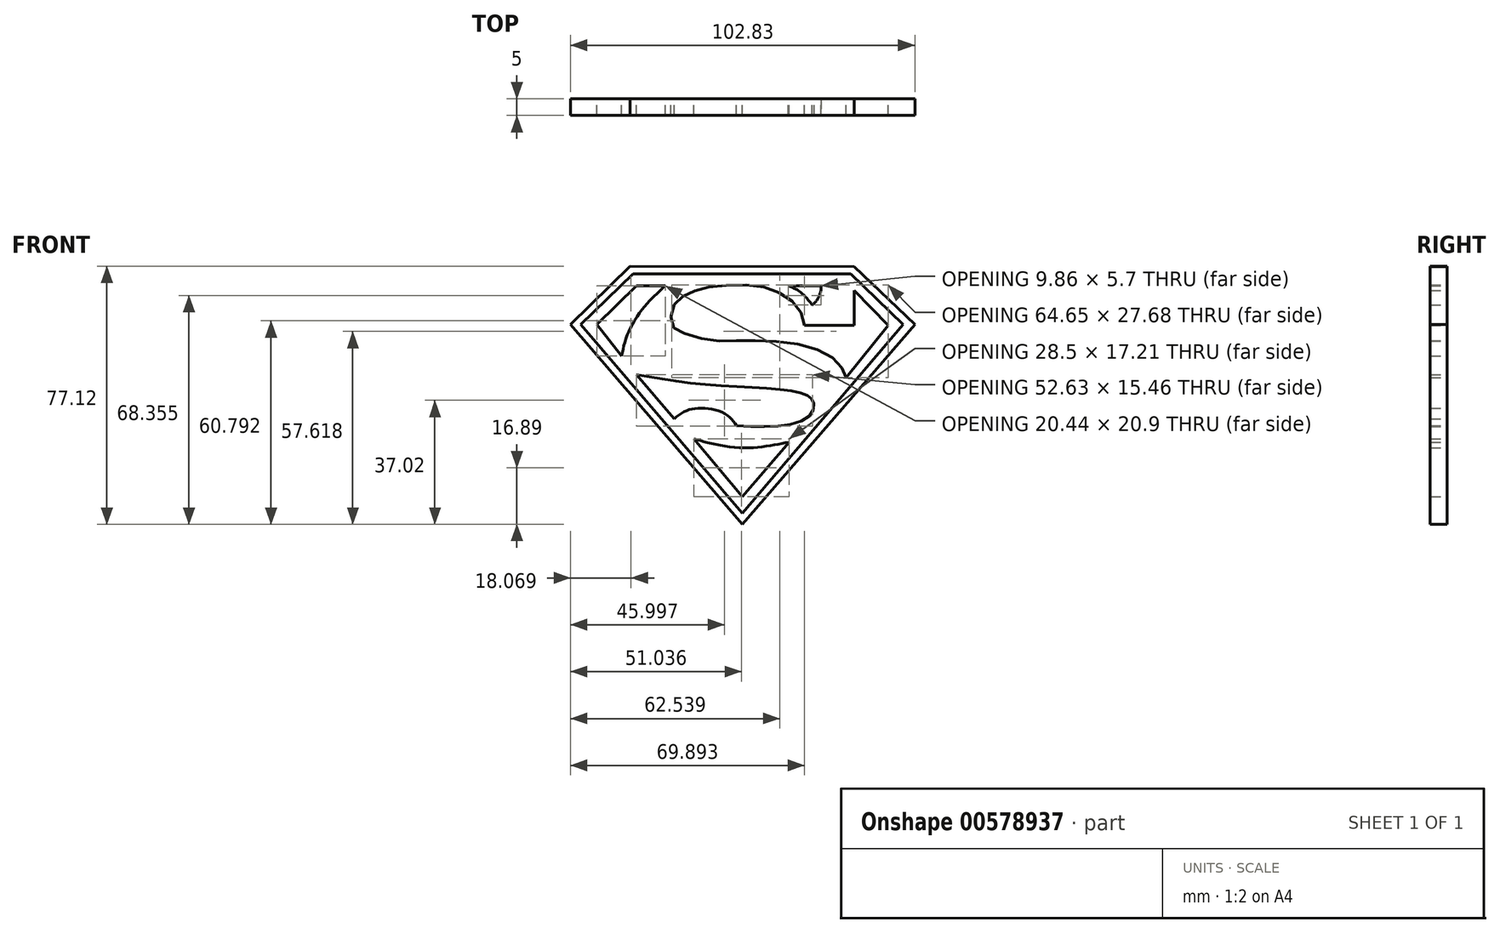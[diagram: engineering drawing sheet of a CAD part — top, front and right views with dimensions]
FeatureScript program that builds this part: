
annotation { "Feature Type Name" : "Feature", "Feature Type Description" : "" }
export const myFeature = defineFeature(function(context is Context, id is Id, definition is map)
    precondition{}
    {
        {
            var Q0;
            Q0=qCreatedBy(makeId("Front.planeOp"),FACE);
            var sketch = newSketch(context, id + "F0", { "sketchPlane" : qUnion([Q0])});
            skFitSpline(sketch, "E0", {"points": [v(-87.65, 79.13) * mm, v(-20.75, 79.03) * mm], "startDerivative": vector(66.9, -0.1) * mm, "endDerivative": vector(66.9, -0.1) * mm});
            skFitSpline(sketch, "E1", {"points": [v(-20.75, 79.03) * mm, v(-2.57, 61.7) * mm], "startDerivative": vector(18.18, -17.32) * mm, "endDerivative": vector(18.18, -17.32) * mm});
            skFitSpline(sketch, "E2", {"points": [v(-87.65, 79.13) * mm, v(-105.4, 61.7) * mm], "startDerivative": vector(-17.75, -17.42) * mm, "endDerivative": vector(-17.75, -17.42) * mm});
            skFitSpline(sketch, "E3", {"points": [v(-105.4, 61.7) * mm, v(-54.1, 2.01) * mm], "startDerivative": vector(51.3, -59.7) * mm, "endDerivative": vector(51.3, -59.7) * mm});
            skFitSpline(sketch, "E4", {"points": [v(-54.1, 2.01) * mm, v(-2.57, 61.7) * mm], "startDerivative": vector(51.52, 59.7) * mm, "endDerivative": vector(51.52, 59.7) * mm});
            skFitSpline(sketch, "E5", {"points": [v(-102.39, 61.7) * mm, v(-86.69, 76.77) * mm], "startDerivative": vector(15.7, 15.06) * mm, "endDerivative": vector(15.7, 15.06) * mm});
            skFitSpline(sketch, "E6", {"points": [v(-86.69, 76.77) * mm, v(-21.72, 76.77) * mm], "startDerivative": vector(64.97, 0) * mm, "endDerivative": vector(64.97, 0) * mm});
            skFitSpline(sketch, "E7", {"points": [v(-21.72, 76.77) * mm, v(-6.12, 61.7) * mm], "startDerivative": vector(15.6, -15.06) * mm, "endDerivative": vector(15.6, -15.06) * mm});
            skFitSpline(sketch, "E8", {"points": [v(-6.12, 61.7) * mm, v(-54.1, 5.35) * mm], "startDerivative": vector(-47.97, -56.36) * mm, "endDerivative": vector(-47.97, -56.36) * mm});
            skFitSpline(sketch, "E9", {"points": [v(-54.1, 5.35) * mm, v(-102.39, 61.7) * mm], "startDerivative": vector(-48.3, 56.36) * mm, "endDerivative": vector(-48.3, 56.36) * mm});
            skFitSpline(sketch, "E10", {"points": [v(-97.55, 61.7) * mm, v(-85.72, 73.25) * mm], "startDerivative": vector(11.83, 11.54) * mm, "endDerivative": vector(11.83, 11.54) * mm});
            skFitSpline(sketch, "E11", {"points": [v(-85.72, 73.25) * mm, v(-77.11, 73.25) * mm], "startDerivative": vector(8.6, 0) * mm, "endDerivative": vector(8.6, 0) * mm});
            skFitSpline(sketch, "E12", {"points": [v(-77.11, 73.25) * mm, v(-80.12, 70.42) * mm, v(-84.53, 65.47) * mm, v(-88.62, 58.05) * mm, v(-90.13, 52.35) * mm], "startDerivative": vector(-14.13, -13.01) * mm, "endDerivative": vector(-4.5, -22.52) * mm});
            skFitSpline(sketch, "E13", {"points": [v(-97.55, 61.7) * mm, v(-90.13, 52.35) * mm], "startDerivative": vector(7.42, -9.36) * mm, "endDerivative": vector(7.42, -9.36) * mm});
            skFitSpline(sketch, "E14", {"points": [v(-85.72, 46.76) * mm, v(-74.42, 33.53) * mm], "startDerivative": vector(11.3, -13.23) * mm, "endDerivative": vector(11.3, -13.23) * mm});
            skFitSpline(sketch, "E15", {"points": [v(-85.72, 46.76) * mm, v(-72.81, 44.6) * mm, v(-55.7, 43.1) * mm, v(-41.19, 42.13) * mm, v(-35.27, 40.73) * mm, v(-33.34, 39.34) * mm, v(-32.7, 37.5) * mm, v(-34.09, 34.39) * mm, v(-42.16, 31.48) * mm, v(-55.82, 31.48) * mm], "startDerivative": vector(87.29, -16.29) * mm, "endDerivative": vector(-97.1, 5.64) * mm});
            skFitSpline(sketch, "E16", {"points": [v(-55.82, 31.48) * mm, v(-57.86, 33.96) * mm, v(-62.16, 36.22) * mm, v(-67.43, 36.65) * mm, v(-71.2, 35.79) * mm, v(-74.42, 33.53) * mm], "startDerivative": vector(-9.96, 14.57) * mm, "endDerivative": vector(-16.14, -13.3) * mm});
            skFitSpline(sketch, "E17", {"points": [v(-68.62, 27.5) * mm, v(-54.1, 10.3) * mm], "startDerivative": vector(14.52, -17.2) * mm, "endDerivative": vector(14.52, -17.2) * mm});
            skFitSpline(sketch, "E18", {"points": [v(-54.1, 10.3) * mm, v(-40.11, 26.54) * mm], "startDerivative": vector(13.98, 16.24) * mm, "endDerivative": vector(13.98, 16.24) * mm});
            skFitSpline(sketch, "E19", {"points": [v(-68.62, 27.5) * mm, v(-63.13, 26.1) * mm, v(-54.1, 24.82) * mm, v(-46.14, 25.46) * mm, v(-40.11, 26.54) * mm], "startDerivative": vector(22.87, -6.27) * mm, "endDerivative": vector(25.29, 4.78) * mm});
            skFitSpline(sketch, "E20", {"points": [v(-33.23, 67.52) * mm, v(-31.72, 69.13) * mm, v(-30.65, 71.82) * mm, v(-30.65, 73.86) * mm], "startDerivative": vector(4.92, 4.4) * mm, "endDerivative": vector(-0.6, 6.28) * mm});
            skFitSpline(sketch, "E21", {"points": [v(-30.58, 73.21) * mm, v(-40.43, 73.21) * mm], "startDerivative": vector(-9.85, 0) * mm, "endDerivative": vector(-9.85, 0) * mm});
            skFitSpline(sketch, "E22", {"points": [v(-40.43, 73.21) * mm, v(-36.89, 71.5) * mm, v(-33.23, 67.52) * mm], "startDerivative": vector(7.92, -2.89) * mm, "endDerivative": vector(6.53, -8.36) * mm});
            skFitSpline(sketch, "E23", {"points": [v(-20.75, 71.82) * mm, v(-20.64, 61.5) * mm], "startDerivative": vector(0.1, -10.33) * mm, "endDerivative": vector(0.1, -10.33) * mm});
            skFitSpline(sketch, "E24", {"points": [v(-20.64, 61.5) * mm, v(-35.6, 61.5) * mm], "startDerivative": vector(-14.95, 0) * mm, "endDerivative": vector(-14.95, 0) * mm});
            skFitSpline(sketch, "E25", {"points": [v(-20.75, 71.82) * mm, v(-10.53, 61.5) * mm], "startDerivative": vector(10.22, -10.33) * mm, "endDerivative": vector(10.22, -10.33) * mm});
            skFitSpline(sketch, "E26", {"points": [v(-10.53, 61.5) * mm, v(-23.12, 45.79) * mm], "startDerivative": vector(-12.58, -15.7) * mm, "endDerivative": vector(-12.58, -15.7) * mm});
            skFitSpline(sketch, "E27", {"points": [v(-23.12, 45.79) * mm, v(-24.62, 49.12) * mm, v(-29.68, 53.32) * mm, v(-41.62, 56.44) * mm, v(-54.42, 56.87) * mm, v(-63.35, 56.98) * mm, v(-72.27, 59.34) * mm, v(-74.96, 61.5) * mm, v(-75.07, 66.12) * mm, v(-72.6, 69.56) * mm, v(-68.19, 71.82) * mm, v(-61.2, 73.21) * mm, v(-49.9, 73.21) * mm, v(-42.59, 70.96) * mm, v(-37.2, 66.33) * mm, v(-35.6, 61.5) * mm], "startDerivative": vector(-23.2, 68.84) * mm, "endDerivative": vector(16.56, -86.92) * mm});
            skFitSpline(sketch, "E28", {"points": [v(-95, 61.42) * mm, v(-84.73, 71.55) * mm], "startDerivative": vector(10.28, 10.13) * mm, "endDerivative": vector(10.28, 10.13) * mm});
            skFitSpline(sketch, "E29", {"points": [v(-84.73, 71.55) * mm, v(-81.6, 71.55) * mm], "startDerivative": vector(3.13, 0) * mm, "endDerivative": vector(3.13, 0) * mm});
            skFitSpline(sketch, "E30", {"points": [v(-81.6, 71.55) * mm, v(-84.73, 67.83) * mm, v(-88.75, 62.02) * mm, v(-90.99, 55.47) * mm], "startDerivative": vector(-10.15, -11.89) * mm, "endDerivative": vector(-4.98, -19) * mm});
            skFitSpline(sketch, "E31", {"points": [v(-95, 61.42) * mm, v(-90.99, 55.47) * mm], "startDerivative": vector(4.02, -5.95) * mm, "endDerivative": vector(4.02, -5.95) * mm});
            skFitSpline(sketch, "E32", {"points": [v(-80.26, 43.85) * mm, v(-74.46, 36.7) * mm], "startDerivative": vector(5.8, -7.15) * mm, "endDerivative": vector(5.8, -7.15) * mm});
            skFitSpline(sketch, "E33", {"points": [v(-74.46, 36.7) * mm, v(-71.2, 37.94) * mm, v(-64.63, 39.23) * mm, v(-56.73, 35.79) * mm, v(-54.35, 33.42) * mm], "startDerivative": vector(14.75, 5.57) * mm, "endDerivative": vector(9.34, -11.21) * mm});
            skFitSpline(sketch, "E34", {"points": [v(-54.35, 33.42) * mm, v(-43.18, 33.42) * mm, v(-36.78, 34.62) * mm, v(-34.24, 37.94) * mm, v(-41.1, 40.13) * mm, v(-55.82, 40.87) * mm, v(-74.46, 42.8) * mm, v(-80.26, 43.85) * mm], "startDerivative": vector(75.42, -0.54) * mm, "endDerivative": vector(-42.21, 8.61) * mm});
            skFitSpline(sketch, "E35", {"points": [v(-63.29, 24.04) * mm, v(-54.35, 13.47) * mm], "startDerivative": vector(8.94, -10.57) * mm, "endDerivative": vector(8.94, -10.57) * mm});
            skFitSpline(sketch, "E36", {"points": [v(-54.35, 13.47) * mm, v(-45.56, 23.45) * mm], "startDerivative": vector(8.79, 9.98) * mm, "endDerivative": vector(8.79, 9.98) * mm});
            skFitSpline(sketch, "E37", {"points": [v(-63.29, 24.04) * mm, v(-54.35, 21.77) * mm, v(-45.56, 23.45) * mm], "startDerivative": vector(17.74, -6.5) * mm, "endDerivative": vector(17.7, 5.34) * mm});
            skFitSpline(sketch, "E38", {"points": [v(-18.9, 67.48) * mm, v(-18.75, 59.49) * mm], "startDerivative": vector(0.15, -8) * mm, "endDerivative": vector(0.15, -8) * mm});
            skFitSpline(sketch, "E39", {"points": [v(-18.75, 59.49) * mm, v(-37.52, 59.49) * mm], "startDerivative": vector(-18.77, 0) * mm, "endDerivative": vector(-18.77, 0) * mm});
            skFitSpline(sketch, "E40", {"points": [v(-18.9, 67.48) * mm, v(-13.1, 61.7) * mm], "startDerivative": vector(5.8, -5.77) * mm, "endDerivative": vector(5.8, -5.77) * mm});
            skFitSpline(sketch, "E41", {"points": [v(-13.1, 61.7) * mm, v(-22.63, 49.66) * mm], "startDerivative": vector(-9.53, -12.05) * mm, "endDerivative": vector(-9.53, -12.05) * mm});
            skFitSpline(sketch, "E42", {"points": [v(-22.63, 49.66) * mm, v(-26.2, 53.68) * mm, v(-34.24, 57.4) * mm, v(-49.43, 59.49) * mm, v(-58.94, 59.49) * mm], "startDerivative": vector(-16.55, 22.32) * mm, "endDerivative": vector(-34.78, -1.05) * mm});
            skFitSpline(sketch, "E43", {"points": [v(-37.52, 59.49) * mm, v(-37.52, 61.7) * mm, v(-39.9, 66.73) * mm, v(-49.43, 71.25) * mm, v(-65.82, 70.66) * mm, v(-72.52, 66.73) * mm, v(-73.11, 62.91) * mm, v(-67, 59.49) * mm, v(-49.43, 59.49) * mm], "startDerivative": vector(3.1, 30.38) * mm, "endDerivative": vector(104.27, 7.97) * mm});
            skSolve(sketch);
        }
        {
            var Q0;
            Q0=makeQuery(id+"F0.imprint","IMPRINT",FACE,{"disambiguationData":[TD([[makeQuery(id+"F0.imprint","IMPRINT",EDGE,{"derivedFrom":sQuery(id+"F0.wireOp",EDGE,"E0")}),-1.0]])]});
            extrude(context, id + "F1", {"entities" : qUnion([Q0]), "depth" : 5 * mm, "offsetDistance" : 25 * mm});
        }
        {
            var Q0;
            Q0=makeQuery(id+"F0.imprint","IMPRINT",FACE,{"disambiguationData":[TD([[makeQuery(id+"F0.imprint","IMPRINT",EDGE,{"derivedFrom":sQuery(id+"F0.wireOp",EDGE,"E5")}),-1.0]])]});
            extrude(context, id + "F2", {"entities" : qUnion([Q0]), "operationType" : NewBodyOperationType.ADD, "depth" : 4.9 * mm, "offsetDistance" : 25 * mm});
        }
    });
